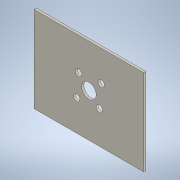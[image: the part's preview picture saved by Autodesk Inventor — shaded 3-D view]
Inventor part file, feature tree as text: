
AUTODESK INVENTOR PART (.ipt)
format: ipt  version: 2022 (Build 260153000, 153)  size: 129,536 bytes
history: native  units: mm
features: sketch x2, sheet_metal_op x1, hole x1, other x1
ambient origin geometry x8: Origin, YZ Plane, XZ Plane, XY Plane, X Axis, Y Axis, Z Axis, Center Point
bodies: Solid1 (feature_tree)
feature tree (5):
  sheet_metal_op  "Face1"
  hole  "Hole2"  [1 undecoded]
  sketch  "Sketch1"  dims[d0=60.0mm d1=47.0mm]
  other  "Plate1"
  sketch  "Sketch3"  dims[d2=8.0mm d3=1.2192mm d15=19.0mm d16=16.0mm d17=45.0deg d18=3.6mm d19=6.0mm d20=6.3mm d21=2.0mm d22=90.0deg d23=1.2192mm d24=20.594885mm]
note: 1 required parameter value undecoded (feature->parameter linkage not recoverable at this tier; creation-order binding heuristic only, values carry confidence <= 0.55)
